# Revit family: 1ICON2_RT_24V_On-wall_86x86_RFA
name_source: partatom
category: Data Devices
units: mm (PartAtom-declared; Revit-internal decimal feet)

## family parameters
Cut with Voids When Loaded = No
Host = Face
Maintain Annotation Orientation = Yes
Part Type = Normal
Room Calculation Point = No
Round Connector Dimension = Use Diameter
Shared = No

## types (1)
- Icon2_RT_24V_On-wall_86x86_088U2128
    BP = 75 mm  [stored 0.246063 ft]
    Body Material = Danfoss Plastic White
    Default Elevation = 0 mm  [stored 0 ft]
    Description = Main Controller and Room Thermostat
    H = 86 mm  [stored 0.282152 ft]
    H2 = 43 mm  [stored 0.141076 ft]
    HH = 82 mm  [stored 0.269029 ft]
    IP Rating = IP 21
    IfcExportAs = IfcElectricApplianceType
    IfcExportType = ICON2_RT_24V
    KR = 15 mm  [stored 0.0492126 ft]
    KR1 = 15 mm  [stored 0.0492126 ft]
    KR2 = 13 mm
    KR3 = 11 mm
    L = 86 mm  [stored 0.282152 ft]
    L2 = 43 mm  [stored 0.141076 ft]
    L2D = 0 mm  [stored 0 ft]
    LL = 82 mm  [stored 0.269029 ft]
    LOD 200 = No
    LOD 350 = Yes
    Manufacturer = Danfoss
    Model = 088U2128
    Model Type = Icon2_RT_24V_On-wall_86x86
    Power = 0 VA
    Power Consumption = 0.2 W
    Power Supply = 24 VDC
    RN = 2 mm  [stored 0.00656168 ft]
    RN1 = 4 mm  [stored 0.0131234 ft]
    SketchPlaneIDs = 10482;153b746f-b00a-47b6-946a-48530699bbd5-000028f2
    URL = https://store.danfoss.com
    Voltage = 24 V
    W = 25 mm  [stored 0.082021 ft]
    W1 = 8 mm  [stored 0.0262467 ft]
    W1__ve = -8 mm  [stored -0.0262467 ft]
    W2D = 0 mm  [stored 0 ft]
    WB = 9 mm  [stored 0.0295276 ft]
    WW = 24 mm  [stored 0.0787402 ft]
    X1 = 26 mm
    XS = 25 mm  [stored 0.082021 ft]
    Z1 = 25 mm  [stored 0.082021 ft]
    Z2 = 24 mm  [stored 0.0787402 ft]
    ZS = 20 mm  [stored 0.0656168 ft]

note: [stored X ft] marks values corroborated as IEEE doubles in the binary element streams (Revit-internal decimal feet)

## geometry (parser evidence)
native form markers: Sweep x1
no freeform markers — native parametric forms only
